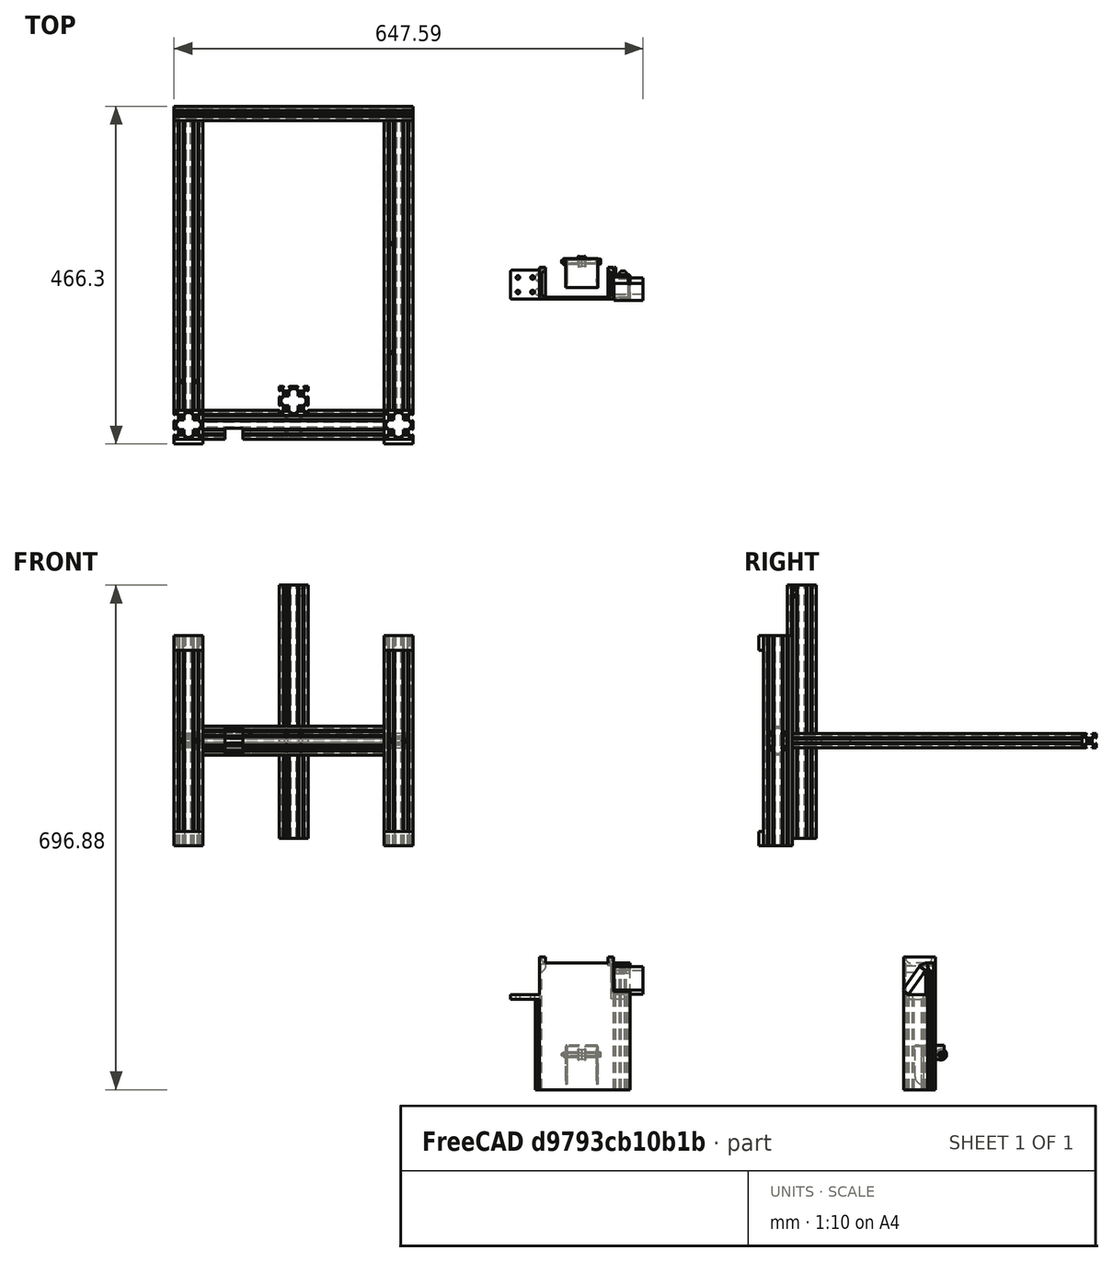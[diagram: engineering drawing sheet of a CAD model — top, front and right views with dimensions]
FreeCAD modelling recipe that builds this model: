
FCSTD DOCUMENT  (FreeCAD 1.1R)
Label: electronic-case-ender3
License: All rights reserved
LicenseURL: https://en.wikipedia.org/wiki/All_rights_reserved
objects: Part::Feature×18, Sketcher::SketchObject×11, PartDesign::Pad×7, PartDesign::Pocket×6, Part::DatumPlane×5, App::Point×3, App::Part×2, PartDesign::SubShapeBinder×2, PartDesign::Fillet×2, Spreadsheet::Sheet×1, Mesh::Feature×1, Part::Box×1, PartDesign::Body×1
note: 89 computed .brp shape members not serialized (recipe doc carries the construction recipe); baked Part::Feature solids carry a one-line shape summary decoded from their .brp

FEATURE [Part::Feature] Part__Feature  label="ЭП-290-4040L"
  Placement = pos=(-524.869,-173.543,336.881) rot=(0,0,1;0rad)
  shape: bbox 40 x 40 x 290 mm, 202 faces (baked)
FEATURE [Part::Feature] Part__Feature001  label="ЭП-290-4040R"
  Placement = pos=(-234.869,-173.543,336.881) rot=(0,0,1;0rad)
  shape: bbox 40 x 40 x 290 mm, 202 faces (baked)
FEATURE [Part::Feature] Part__Feature002  label="ЭП-250-4040D"
  Placement = pos=(-254.869,-173.543,481.881) rot=(0,-1,0;1.5708rad)
  shape: bbox 250 x 40 x 40 mm, 268 faces (baked)
FEATURE [Part::Feature] Part__Feature003  label="ЭП-400-2040L"
  Placement = pos=(-524.869,-153.543,481.881) rot=(-1,0,0;1.5708rad)
  shape: bbox 40 x 400 x 20 mm, 84 faces (baked)
FEATURE [Part::Feature] Part__Feature004  label="ЭП-400-2040R"
  Placement = pos=(-234.869,246.457,481.881) rot=(0,0.707107,-0.707107;3.14159rad)
  shape: bbox 40 x 400 x 20 mm, 92 faces (baked)
FEATURE [Part::Feature] Part__Feature005  label="ЭП-330-2020"
  Placement = pos=(-214.869,256.457,481.881) rot=(0,-1,0;1.5708rad)
  shape: bbox 330 x 20 x 20 mm, 87 faces (baked)
FEATURE [Part::Feature] Part__Feature006  label="ЭП-350-4040C"
  Placement = pos=(-379.869,-140.543,346.881) rot=(0,0,1;0rad)
  shape: bbox 40 x 40 x 350 mm, 142 faces (baked)
FEATURE [Part::Feature] Part__Feature161  label="Дистанционная_шайба_натяжителя"
  Placement = pos=(-1.75288,51.8974,48.5) rot=(0,1,0;1.5708rad)
  shape: bbox 15 x 7.1 x 7.1 mm, 4 faces (baked)
FEATURE [Part::Feature] Part__Feature162  label="Кронштейн_натяжного_ролика"
  Placement = pos=(18.1071,35.9974,59.5) rot=(0,0,1;0rad)
  shape: bbox 44.3 x 40.2 x 54.1 mm, 32 faces (baked)
FEATURE [Part::Feature] Part__Feature163  label="Направляющий_ролик002"
  Placement = pos=(22.9671,51.8974,48.5) rot=(0,-1,0;1.5708rad)
  shape: bbox 4.86 x 15 x 15 mm, 15 faces (baked)
FEATURE [Part::Feature] Part__Feature164  label="Направляющий_ролик003"
  Placement = pos=(13.2471,51.8974,48.5) rot=(0,1,0;1.5708rad)
  shape: bbox 4.86 x 15 x 15 mm, 15 faces (baked)
FEATURE [Part::Feature] Part__Feature165  label="Дистанционная_шайба_натяжителя001"
  Placement = pos=(37.9671,51.8974,48.5) rot=(0,-1,0;1.5708rad)
  shape: bbox 15 x 7.1 x 7.1 mm, 4 faces (baked)
FEATURE [Part::Feature] Part__Feature166  label="CNS 3932 - M 4 x 0,7 x 50"
  Placement = pos=(40.2571,51.8974,48.5) rot=(0,0,1;3.14159rad)
  shape: bbox 54 x 7.577 x 7.577 mm, 15 faces (baked)
FEATURE [Part::Feature] Part__Feature167  label="AS 1112 - M4  Тип 5"
  Placement = pos=(-7.24288,51.8974,48.5) rot=(0,0,1;0rad)
  shape: bbox 3.2 x 8.083 x 8.083 mm, 23 faces (baked)
FEATURE [App::Part] _________________________________________  label="Натяжной_ролик_в_сборе"
  Group = -> [Part__Feature161,Part__Feature162,Part__Feature163,Part__Feature164,Part__Feature165,Part__Feature166,Part__Feature167]
  Origin = -> Origin032
  Placement = pos=(-397.926,-176.441,657.381) rot=(0,0,1;0rad)
FEATURE [App::Point] Origin033
  Role = Origin
FEATURE [Part::Feature] Part__Feature275  label="Резиновые_ножки"
  Placement = pos=(-234.869,-199.843,616.881) rot=(-1,0,0;1.5708rad)
  shape: bbox 40 x 6.3 x 20 mm, 6 faces (baked)
FEATURE [Part::Feature] Part__Feature276  label="Резиновые_ножки001"
  Placement = pos=(-524.869,-193.543,346.881) rot=(1,0,0;1.5708rad)
  shape: bbox 40 x 6.3 x 20 mm, 6 faces (baked)
FEATURE [Part::Feature] Part__Feature277  label="Резиновые_ножки002"
  Placement = pos=(-234.869,-199.843,346.881) rot=(-1,0,0;1.5708rad)
  shape: bbox 40 x 6.3 x 20 mm, 6 faces (baked)
FEATURE [Part::Feature] Part__Feature278  label="Резиновые_ножки003"
  Placement = pos=(-524.869,-193.543,616.881) rot=(1,0,0;1.5708rad)
  shape: bbox 40 x 6.3 x 20 mm, 6 faces (baked)
FEATURE [App::Part] ________  label="Рама"
  Group = -> [Part__Feature,Part__Feature001,Part__Feature002,Part__Feature003,Part__Feature004,Part__Feature005,Part__Feature006,_________________________________________,Part__Feature275,Part__Feature276,Part__Feature277,Part__Feature278]
  Origin = -> Origin052
  Placement = pos=(464.817,193.554,-501.882) rot=(0,0,1;0rad)
FEATURE [App::Point] Origin053
  Role = Origin
FEATURE [App::Point] Origin055
  Role = Origin
FEATURE [Sketcher::SketchObject] Sketch
  ArcFitTolerance = 1e-06
  AttachmentSupport = -> [Origin054]
  ExternalTypes = [0]
  FullyConstrained = false
  MakeInternals = false
  MapMode = 5
  sketch-geometry (56):
    g0: LineSegment StartX=78 StartY=32.9 StartZ=0 EndX=78 EndY=35 EndZ=0
    g1: LineSegment StartX=77.4 StartY=39.1 StartZ=0 EndX=72.6 EndY=39.1 EndZ=0
    g2: LineSegment StartX=70 StartY=35 StartZ=0 EndX=72 EndY=35 EndZ=0
    g3: LineSegment StartX=78 StartY=35 StartZ=0 EndX=80 EndY=35 EndZ=0
    g4: LineSegment StartX=70 StartY=35 StartZ=0 EndX=70 EndY=36.5 EndZ=0
    g5: LineSegment StartX=70 StartY=36.5 StartZ=0 EndX=72.6 EndY=39.1 EndZ=0
    g6: LineSegment StartX=77.4 StartY=39.1 StartZ=0 EndX=80 EndY=36.5 EndZ=0
    g7: LineSegment StartX=80 StartY=36.5 StartZ=0 EndX=80 EndY=35 EndZ=0
    g8: LineSegment [constr] StartX=70 StartY=36.5 StartZ=0 EndX=80 EndY=36.5 EndZ=0
    g9: LineSegment StartX=-40 StartY=11.8 StartZ=0 EndX=-42 EndY=11.8 EndZ=0
    g10: LineSegment StartX=-46.1 StartY=12.1 StartZ=0 EndX=-46.1 EndY=7.6 EndZ=0
    g11: LineSegment StartX=-42 StartY=7.9 StartZ=0 EndX=-40 EndY=7.9 EndZ=0
    g12: LineSegment StartX=-42 StartY=5 StartZ=0 EndX=-43.5 EndY=5 EndZ=0
    g13: LineSegment [constr] StartX=-43.5 StartY=5 StartZ=0 EndX=-43.5 EndY=15 EndZ=0
    g14: LineSegment StartX=-40 StartY=7.9 StartZ=0 EndX=-40 EndY=0 EndZ=0
    g15: LineSegment [constr] StartX=72 StartY=35 StartZ=0 EndX=75 EndY=35 EndZ=0
    g16: LineSegment [constr] StartX=75 StartY=35 StartZ=0 EndX=78 EndY=35 EndZ=0
    g17: LineSegment [constr] StartX=75 StartY=35 StartZ=0 EndX=75 EndY=0 EndZ=0
    g18: LineSegment StartX=-40 StartY=11.8 StartZ=0 EndX=-40 EndY=27.8 EndZ=0
    g19: LineSegment StartX=-37 StartY=16 StartZ=0 EndX=-37 EndY=41.5 EndZ=0
    g20: LineSegment StartX=-40 StartY=44 StartZ=0 EndX=-40 EndY=32 EndZ=0
    g21: LineSegment StartX=-40 StartY=32 StartZ=0 EndX=-42 EndY=32 EndZ=0
    g22: LineSegment StartX=-42 StartY=32 StartZ=0 EndX=-42 EndY=34.9 EndZ=0
    g23: LineSegment StartX=-42 StartY=34.9 StartZ=0 EndX=-43.5 EndY=34.9 EndZ=0
    g24: LineSegment StartX=-43.5 StartY=34.9 StartZ=0 EndX=-46.1 EndY=32.15 EndZ=0
    g25: LineSegment StartX=-46.1 StartY=32.15 StartZ=0 EndX=-46.1 EndY=27.65 EndZ=0
    g26: LineSegment StartX=-46.1 StartY=27.65 StartZ=0 EndX=-43.5 EndY=24.9 EndZ=0
    g27: LineSegment StartX=-43.5 StartY=24.9 StartZ=0 EndX=-42 EndY=24.9 EndZ=0
    g28: LineSegment StartX=-42 StartY=24.9 StartZ=0 EndX=-42 EndY=27.8 EndZ=0
    g29: LineSegment StartX=-42 StartY=27.8 StartZ=0 EndX=-40 EndY=27.8 EndZ=0
    g30: LineSegment StartX=-37 StartY=41.5 StartZ=0 EndX=-38.5 EndY=41.5 EndZ=0
    g31: LineSegment StartX=-38.5 StartY=41.5 StartZ=0 EndX=-38.5 EndY=44 EndZ=0
    g32: LineSegment StartX=-38.5 StartY=44 StartZ=0 EndX=-40 EndY=44 EndZ=0
    g33: LineSegment [constr] StartX=-43.5 StartY=34.9 StartZ=0 EndX=-43.5 EndY=24.9 EndZ=0
    g34: LineSegment StartX=-37 StartY=16 StartZ=0 EndX=-37 EndY=2.5 EndZ=0
    g35: LineSegment StartX=-37 StartY=2.5 StartZ=0 EndX=82.5 EndY=2.5 EndZ=0
    g36: LineSegment [constr] StartX=72 StartY=35 StartZ=0 EndX=72 EndY=2.5 EndZ=0
    g37: LineSegment StartX=63.4 StartY=44 StartZ=0 EndX=64.9 EndY=44 EndZ=0
    g38: LineSegment StartX=64.9 StartY=44 StartZ=0 EndX=64.9 EndY=32.9 EndZ=0
    g39: LineSegment StartX=64.9 StartY=32.9 StartZ=0 EndX=72 EndY=32.9 EndZ=0
    g40: LineSegment StartX=63.4 StartY=44 StartZ=0 EndX=63.4 EndY=41.5 EndZ=0
    g41: LineSegment StartX=63.4 StartY=41.5 StartZ=0 EndX=61.9 EndY=41.5 EndZ=0
    g42: LineSegment StartX=61.9 StartY=41.5 StartZ=0 EndX=61.9 EndY=32.9 EndZ=0
    g43: LineSegment StartX=61.9 StartY=32.9 StartZ=0 EndX=61.9 EndY=30.4 EndZ=0
    g44: LineSegment StartX=61.9 StartY=30.4 StartZ=0 EndX=72 EndY=30.4 EndZ=0
    g45: LineSegment StartX=72 StartY=35 StartZ=0 EndX=72 EndY=32.9 EndZ=0
    g46: LineSegment StartX=78 StartY=32.9 StartZ=0 EndX=85 EndY=32.9 EndZ=0
    g47: LineSegment StartX=85 StartY=32.9 StartZ=0 EndX=85 EndY=0 EndZ=0
    g48: LineSegment StartX=-40 StartY=0 StartZ=0 EndX=85 EndY=0 EndZ=0
    g49: LineSegment StartX=-43.5 StartY=5 StartZ=0 EndX=-46.1 EndY=7.6 EndZ=0
    g50: LineSegment StartX=-46.1 StartY=12.1 StartZ=0 EndX=-43.5 EndY=14.7 EndZ=0
    g51: LineSegment StartX=-43.5 StartY=14.7 StartZ=0 EndX=-42 EndY=14.7 EndZ=0
    g52: LineSegment StartX=-42 StartY=14.7 StartZ=0 EndX=-42 EndY=11.8 EndZ=0
    g53: LineSegment StartX=-42 StartY=7.9 StartZ=0 EndX=-42 EndY=5 EndZ=0
    g54: LineSegment StartX=72 StartY=30.4 StartZ=0 EndX=82.5 EndY=30.4 EndZ=0
    g55: LineSegment StartX=82.5 StartY=30.4 StartZ=0 EndX=82.5 EndY=2.5 EndZ=0
  constraints (164):
    c: Vertical(g0)
    c: Horizontal(g2)
    c: Coincident(g3,g0)
    c: Horizontal(g3,g0)
    c: Horizontal(g0,g2)
    c: Equal(g2,g3)
    c: DistanceX(g2,g3) = 10
    c: Coincident(g4,g2)
    c: Coincident(g4,g5)
    c: Coincident(g5,g1)
    c: Coincident(g6,g1)
    c: Coincident(g6,g7)
    c: Coincident(g7,g3)
    c: Parallel(g7,g4)
    c: Equal(g7,g4)
    c: Angle(g5,g6) = 1.5708
    c: Perpendicular(g2,g4)
    c: Coincident(g8,g4)
    c: Coincident(g8,g6)
    c: Angle(g8,g5) = 0.785398
    c: DistanceY(g7,g7) = 1.5
    c: Horizontal(g1)
    c: Distance(g3,g1) = 4.1
    c: Coincident(g13,g12)
    c: Distance(g9,g10) = 4.1
    c: Coincident(g14,g11)
    c: DistanceX(g11,g11) = 2
    c: Perpendicular(g14,g11)
    c: Vertical(g11,g9)
    c: Distance(g12,g-1) = 5
    c: DistanceY(g12,g13) = 10
    c: Distance(g-1,g14) = 40
    c: Coincident(g15,g2)
    c: Horizontal(g15)
    c: Coincident(g15,g16)
    c: Coincident(g16,g0)
    c: Equal(g15,g16)
    c: Coincident(g17,g15)
    c: Vertical(g17)
    c: Distance(g14,g17) = 115
    c: Equal(g9,g11)
    c: Coincident(g18,g9)
    c: Vertical(g18)
    c: Vertical(g19)
    c: Vertical(g20)
    c: Coincident(g20,g21)
    c: Coincident(g21,g22)
    c: Vertical(g22)
    c: Coincident(g22,g23)
    c: Coincident(g23,g24)
    c: Coincident(g24,g25)
    c: Vertical(g25)
    c: Coincident(g25,g26)
    c: Coincident(g26,g27)
    c: Horizontal(g27)
    c: Coincident(g27,g28)
    c: Coincident(g28,g29)
    c: Coincident(g29,g18)
    c: Perpendicular(g20,g21)
    c: Perpendicular(g18,g29)
    c: Coincident(g30,g19)
    c: Parallel(g30,g23)
    c: Coincident(g30,g31)
    c: Vertical(g31)
    c: Coincident(g31,g32)
    c: Coincident(g32,g20)
    c: Parallel(g32,g30)
    c: Horizontal(g32)
    c: Equal(g30,g32)
    c: Vertical(g18,g20)
    c: Perpendicular(g29,g28)
    c: Coincident(g33,g23)
    c: Coincident(g33,g26)
    c: Vertical(g33)
    c: Equal(g33,g13)
    c: DistanceY(g31,g31) = 2.5
    c: Equal(g24,g26)
    c: Equal(g25,g10)
    c: Vertical(g25,g10)
    c: Vertical(g23,g13)
    c: Vertical(g21,g28)
    c: DistanceY(g18,g18) = 16
    c: DistanceY(g20,g20) = 12
    c: DistanceY(g19,g19) = 25.5
    c: Coincident(g34,g19)
    c: Vertical(g34)
    c: Coincident(g34,g35)
    c: Horizontal(g35)
    c: Coincident(g36,g2)
    c: Parallel(g0,g36)
    c: Distance(g34,g14) = 3
    c: DistanceX(g2,g0) = 6
    c: Perpendicular(g18,g9)
    c: Vertical(g10)
    c: PointOnObject(g44,g36)
    c: Coincident(g37,g38)
    c: Coincident(g38,g39)
    c: PointOnObject(g39,g36)
    c: Horizontal(g39)
    c: Horizontal(g31,g37)
    c: Horizontal(g37)
    c: Vertical(g38)
    c: Coincident(g40,g37)
    c: Vertical(g40)
    c: Coincident(g40,g41)
    c: Coincident(g41,g42)
    c: Vertical(g42)
    c: Coincident(g42,g43)
    c: Vertical(g43)
    c: Coincident(g43,g44)
    c: Perpendicular(g41,g40)
    c: Distance(g38,g42) = 3
    c: Equal(g41,g37)
    c: Distance(g2,g39) = 2.1
    c: DistanceX(g39,g39) = 7.1
    c: Equal(g40,g31)
    c: Horizontal(g42,g38)
    c: DistanceY(g43,g43) = 2.5
    c: Coincident(g45,g2)
    c: Coincident(g45,g39)
    c: Horizontal(g0,g39)
    c: Coincident(g46,g0)
    c: Horizontal(g46)
    c: Coincident(g46,g47)
    c: PointOnObject(g47,g-1)
    c: Vertical(g47)
    c: DistanceX(g17,g47) = 10
    c: Vertical(g14)
    c: PointOnObject(g14,g-1)
    c: Distance(g-1,g35) = 2.5
    c: DistanceY(g38,g38) = 11.1
    c: Coincident(g48,g14)
    c: Coincident(g48,g47)
    c: Coincident(g49,g12)
    c: Coincident(g49,g10)
    c: Coincident(g50,g10)
    c: Distance(g31,g48) = 44
    c: PointOnObject(g17,g48)
    c: DistanceY(g25,g25) = 4.5
    c: Coincident(g51,g50)
    c: Horizontal(g51)
    c: Coincident(g52,g51)
    c: Coincident(g52,g9)
    c: Vertical(g52)
    c: Coincident(g53,g11)
    c: Coincident(g53,g12)
    c: Vertical(g53)
    c: Vertical(g28,g9)
    c: Equal(g53,g52)
    c: Equal(g52,g28)
    c: Perpendicular(g53,g12)
    c: Equal(g49,g50)
    c: Vertical(g13)
    c: Equal(g51,g12)
    c: DistanceX(g51,g51) = 1.5
    c: Equal(g22,g28)
    c: Angle(g13,g49) = 0.785398
    c: Coincident(g54,g44)
    c: Horizontal(g54)
    c: Coincident(g55,g54)
    c: Coincident(g55,g35)
    c: Perpendicular(g55,g54)
    c: Distance(g47,g55) = 2.5
    c: Horizontal(g44)
FEATURE [PartDesign::Pad] Pad
  Direction = (0,0,1)
  Length = 175
  Length2 = 10
  Profile = -> Sketch
  ReferenceAxis = -> Sketch [N_Axis]
  Refine = true
  SideType = 0
  Suppressed = false
  Type = 0
  Type2 = 0
  expr: Length = 125 + Spreadsheet.stickout
FEATURE [Part::DatumPlane] DatumPlane001
  AttachmentSupport = -> [Pad]
  MapMode = 1
  Placement = pos=(-40,44,175) rot=(0,0,1;0rad)
FEATURE [Sketcher::SketchObject] Sketch001
  ArcFitTolerance = 1e-06
  AttachmentSupport = -> [DatumPlane001]
  ExternalTypes = [0]
  FullyConstrained = true
  MakeInternals = false
  MapMode = 5
  Placement = pos=(-40,44,175) rot=(0,0,1;0rad)
  sketch-geometry (10):
    g0: LineSegment StartX=0 StartY=-4 StartZ=0 EndX=-38.5858 EndY=-4 EndZ=0
    g1: LineSegment StartX=-40 StartY=-5.41421 StartZ=0 EndX=-40 EndY=-42.5858 EndZ=0
    g2: LineSegment StartX=-38.5858 StartY=-44 StartZ=0 EndX=0 EndY=-44 EndZ=0
    g3: ArcOfCircle CenterX=-38.5858 CenterY=-5.41421 CenterZ=0 NormalX=0 NormalY=0 NormalZ=1 AngleXU=0 Radius=1.41421 StartAngle=1.5708 EndAngle=3.14159
    g4: GeomPoint [constr] X=-40 Y=-4 Z=0
    g5: LineSegment [constr] StartX=-38.5858 StartY=-4 StartZ=0 EndX=-40 EndY=-5.41421 EndZ=0
    g6: ArcOfCircle CenterX=-38.5858 CenterY=-42.5858 CenterZ=0 NormalX=0 NormalY=0 NormalZ=1 AngleXU=0 Radius=1.41421 StartAngle=3.14159 EndAngle=4.71239
    g7: GeomPoint [constr] X=-40 Y=-44 Z=0
    g8: LineSegment [constr] StartX=-40 StartY=-42.5858 StartZ=0 EndX=-38.5858 EndY=-44 EndZ=0
    g9: LineSegment StartX=0 StartY=-44 StartZ=0 EndX=0 EndY=-4 EndZ=0
  constraints (24):
    c: Horizontal(g0)
    c: Horizontal(g2)
    c: Vertical(g1)
    c: DistanceY(g7,g4) = 40
    c: PointOnObject(g4,g0)
    c: PointOnObject(g4,g1)
    c: Tangent(g0,g3) = -1.5708
    c: Tangent(g1,g3) = -1.5708
    c: Coincident(g5,g0)
    c: Coincident(g5,g1)
    c: PointOnObject(g7,g1)
    c: PointOnObject(g7,g2)
    c: Tangent(g1,g6) = -1.5708
    c: Tangent(g2,g6) = -1.5708
    c: Coincident(g8,g1)
    c: Coincident(g8,g2)
    c: Equal(g8,g5)
    c: Distance(g5,g5) = 2
    c: DistanceX(g7,g2) = 40
    c: Coincident(g9,g2)
    c: PointOnObject(g9,g-2)
    c: Vertical(g9)
    c: Coincident(g0,g9)
    c: Distance(g-1,g0) = 4
FEATURE [PartDesign::Pad] Pad001
  BaseFeature = -> Pad
  Direction = (0,0,1)
  Length = 50.001
  Length2 = 10
  Profile = -> Sketch001
  ReferenceAxis = -> Sketch001 [N_Axis]
  Refine = true
  Reversed = true
  SideType = 0
  Suppressed = false
  Type = 0
  Type2 = 0
  expr: Length = Spreadsheet.stickout + 0.001
FEATURE [Sketcher::SketchObject] Sketch002
  ArcFitTolerance = 1e-06
  AttachmentSupport = -> [DatumPlane001]
  ExternalTypes = [0]
  FullyConstrained = true
  MakeInternals = false
  MapMode = 5
  Placement = pos=(-40,44,175) rot=(0,0,1;0rad)
  sketch-geometry (4):
    g0: LineSegment StartX=0 StartY=0 StartZ=0 EndX=-44 EndY=0 EndZ=0
    g1: LineSegment StartX=-44 StartY=0 StartZ=0 EndX=-44 EndY=-44 EndZ=0
    g2: LineSegment StartX=-44 StartY=-44 StartZ=0 EndX=0 EndY=-44 EndZ=0
    g3: LineSegment StartX=0 StartY=-44 StartZ=0 EndX=0 EndY=0 EndZ=0
  constraints (11):
    c: Coincident(g0,g1)
    c: Coincident(g1,g2)
    c: Coincident(g2,g3)
    c: Coincident(g3,g0)
    c: Horizontal(g0)
    c: Horizontal(g2)
    c: Vertical(g1)
    c: Vertical(g3)
    c: Coincident(g0,g-1)
    c: Equal(g1,g0)
    c: DistanceY(g1,g1) = 44
FEATURE [Spreadsheet::Sheet] Spreadsheet
  cells = B1(stickout)=50
FEATURE [PartDesign::Pocket] Pocket
  BaseFeature = -> Pad001
  Direction = (0,0,-1)
  Length = 44.001
  Length2 = 5
  Profile = -> Sketch002
  ReferenceAxis = -> Sketch002 [N_Axis]
  Refine = true
  SideType = 0
  Suppressed = false
  Type = 0
  Type2 = 0
  expr: Length = Spreadsheet.stickout - 6 + 0.001
FEATURE [Sketcher::SketchObject] Sketch003
  ArcFitTolerance = 1e-06
  AttachmentSupport = -> [DatumPlane001]
  ExternalTypes = [0]
  FullyConstrained = true
  MakeInternals = false
  MapMode = 5
  Placement = pos=(-40,44,175) rot=(0,0,1;0rad)
  sketch-geometry (8):
    g0: Circle CenterX=-10 CenterY=-14 CenterZ=0 NormalX=0 NormalY=0 NormalZ=1 AngleXU=0 Radius=2.5
    g1: Circle CenterX=-30 CenterY=-14 CenterZ=0 NormalX=0 NormalY=0 NormalZ=1 AngleXU=0 Radius=2.5
    g2: Circle CenterX=-30 CenterY=-34 CenterZ=0 NormalX=0 NormalY=0 NormalZ=1 AngleXU=0 Radius=2.5
    g3: Circle CenterX=-10 CenterY=-34 CenterZ=0 NormalX=0 NormalY=0 NormalZ=1 AngleXU=0 Radius=2.5
    g4: LineSegment [constr] StartX=-30 StartY=-14 StartZ=0 EndX=-10 EndY=-14 EndZ=0
    g5: LineSegment [constr] StartX=-10 StartY=-14 StartZ=0 EndX=-10 EndY=-34 EndZ=0
    g6: LineSegment [constr] StartX=-10 StartY=-34 StartZ=0 EndX=-30 EndY=-34 EndZ=0
    g7: LineSegment [constr] StartX=-30 StartY=-34 StartZ=0 EndX=-30 EndY=-14 EndZ=0
  constraints (20):
    c: Diameter(g0) = 5
    c: Equal(g1,g0)
    c: Equal(g0,g3)
    c: Equal(g3,g2)
    c: Coincident(g4,g1)
    c: Coincident(g4,g0)
    c: Horizontal(g4)
    c: Coincident(g4,g5)
    c: Coincident(g5,g3)
    c: Vertical(g5)
    c: Coincident(g5,g6)
    c: Coincident(g6,g2)
    c: Horizontal(g6)
    c: Coincident(g6,g7)
    c: Coincident(g7,g1)
    c: Vertical(g7)
    c: Equal(g7,g4)
    c: Distance(g0,g-2) = 10
    c: Distance(g0,g-1) = 14
    c: DistanceX(g4,g4) = 20
FEATURE [PartDesign::Pocket] Pocket001
  BaseFeature = -> Pocket
  Direction = (0,0,-1)
  Length = 500
  Length2 = 5
  Profile = -> Sketch003
  ReferenceAxis = -> Sketch003 [N_Axis]
  Refine = true
  SideType = 0
  Suppressed = false
  Type = 0
  Type2 = 0
FEATURE [Mesh::Feature] Headless_Skirt_Insert
  Placement = pos=(-207.979,-60.019,-95.105) rot=(0,0,1;0rad)
FEATURE [PartDesign::SubShapeBinder] Binder
  BindCopyOnChange = 0
  BindMode = 0
  ClaimChildren = false
  Context = -> Body [Pad003.Binder.]
  Fuse = false
  MakeFace = true
  OffsetFill = false
  OffsetIntersection = false
  OffsetJoinType = 0
  OffsetOpenResult = false
  PartialLoad = false
  Placement = pos=(102,0,0) rot=(0,0,1;0rad)
  Relative = true
  Support = -> [Sketch005]
  _Version = 2
FEATURE [PartDesign::SubShapeBinder] Binder001
  BindCopyOnChange = 0
  BindMode = 0
  ClaimChildren = false
  Context = -> Body [Binder001.]
  Fuse = false
  MakeFace = true
  OffsetFill = false
  OffsetIntersection = false
  OffsetJoinType = 0
  OffsetOpenResult = false
  PartialLoad = false
  Placement = pos=(86,0,0) rot=(0,0,1;0rad)
  Refine = true
  Relative = true
  Support = -> [Sketch006]
  _Version = 2
FEATURE [Part::Box] Box  label="Cube"
  AttacherType = Attacher::AttachEngine3D
  Height = 40
  Length = 10
  Placement = pos=(102.724,21.5401,170.201) rot=(0.663579,0.345437,-0.663579;3.8068rad)
  Width = 40
FEATURE [Part::DatumPlane] DatumPlane
  AttachmentOffset = pos=(0,0,0) rot=(0.57735,0.57735,0.57735;2.0944rad)
  AttachmentSupport = -> [Pocket001]
  MapMode = 7
  Placement = pos=(-40,0,175) rot=(0.57735,0.57735,0.57735;2.0944rad)
FEATURE [Sketcher::SketchObject] Sketch005
  ArcFitTolerance = 1e-06
  AttachmentSupport = -> [DatumPlane]
  ExternalTypes = [0]
  FullyConstrained = true
  MakeInternals = false
  MapMode = 5
  Placement = pos=(-40,0,175) rot=(0.57735,0.57735,0.57735;2.0944rad)
  sketch-geometry (8):
    g0: LineSegment [constr] StartX=0 StartY=-4 StartZ=0 EndX=44 EndY=-4 EndZ=0
    g1: LineSegment [constr] StartX=44 StartY=-4 StartZ=0 EndX=44 EndY=8 EndZ=0
    g2: LineSegment StartX=44 StartY=8 StartZ=0 EndX=0 EndY=8 EndZ=0
    g3: LineSegment StartX=0 StartY=8 StartZ=0 EndX=0 EndY=-4 EndZ=0
    g4: LineSegment StartX=0 StartY=-4 StartZ=0 EndX=41.5 EndY=-4 EndZ=0
    g5: LineSegment StartX=41.5 StartY=-4 StartZ=0 EndX=41.5 EndY=-1 EndZ=0
    g6: LineSegment StartX=41.5 StartY=-1 StartZ=0 EndX=44 EndY=-1 EndZ=0
    g7: LineSegment StartX=44 StartY=-1 StartZ=0 EndX=44 EndY=8 EndZ=0
  constraints (23):
    c: Coincident(g0,g1)
    c: Coincident(g1,g2)
    c: Coincident(g2,g3)
    c: Coincident(g3,g0)
    c: Horizontal(g0)
    c: Horizontal(g2)
    c: Vertical(g1)
    c: Vertical(g3)
    c: PointOnObject(g0,g-2)
    c: DistanceY(g1,g1) = 12
    c: Distance(g-1,g0) = 4
    c: DistanceX(g2,g2) = 44
    c: Coincident(g4,g0)
    c: PointOnObject(g4,g0)
    c: Coincident(g4,g5)
    c: Vertical(g5)
    c: Coincident(g5,g6)
    c: PointOnObject(g6,g1)
    c: Horizontal(g6)
    c: Coincident(g6,g7)
    c: Coincident(g7,g1)
    c: Distance(g6,g0) = 3
    c: DistanceX(g6,g6) = 2.5
FEATURE [PartDesign::Pad] Pad002
  BaseFeature = -> Pocket001
  Direction = (1,0,0)
  Length = 8
  Length2 = 10
  Profile = -> Sketch005
  ReferenceAxis = -> Sketch005 [N_Axis]
  Refine = true
  SideType = 0
  Suppressed = false
  Type = 0
  Type2 = 0
FEATURE [PartDesign::Pad] Pad003
  BaseFeature = -> Pad002
  Direction = (1,0,0)
  Length = 8
  Length2 = 10
  Profile = -> Binder
  Refine = true
  Reversed = true
  SideType = 0
  Suppressed = false
  Type = 0
  Type2 = 0
FEATURE [Sketcher::SketchObject] Sketch006
  ArcFitTolerance = 1e-06
  AttachmentOffset = pos=(0,0,8) rot=(0,0,1;0rad)
  AttachmentSupport = -> [DatumPlane]
  ExternalTypes = [0]
  FullyConstrained = true
  MakeInternals = false
  MapMode = 5
  Placement = pos=(-32,0,175) rot=(0.57735,0.57735,0.57735;2.0944rad)
  sketch-geometry (6):
    g0: ArcOfCircle CenterX=32.5 CenterY=6.5 CenterZ=0 NormalX=0 NormalY=0 NormalZ=1 AngleXU=0 Radius=6.5 StartAngle=4.71239 EndAngle=6.28319
    g1: ArcOfCircle CenterX=9.5 CenterY=6.5 CenterZ=0 NormalX=0 NormalY=0 NormalZ=1 AngleXU=0 Radius=6.5 StartAngle=3.14159 EndAngle=4.71239
    g2: LineSegment StartX=39 StartY=6.5 StartZ=0 EndX=39 EndY=8 EndZ=0
    g3: LineSegment StartX=39 StartY=8 StartZ=0 EndX=3 EndY=8 EndZ=0
    g4: LineSegment StartX=3 StartY=8 StartZ=0 EndX=3 EndY=6.5 EndZ=0
    g5: LineSegment StartX=32.5 StartY=0 StartZ=0 EndX=9.5 EndY=0 EndZ=0
  constraints (16):
    c: Vertical(g2)
    c: Coincident(g2,g3)
    c: Horizontal(g3)
    c: Coincident(g3,g4)
    c: DistanceX(g3,g3) = 36
    c: Vertical(g4)
    c: Equal(g4,g2)
    c: Tangent(g1,g-1) = -1.5708
    c: Tangent(g2,g0) = -1.5708
    c: Tangent(g4,g1) = -1.5708
    c: Tangent(g0,g-1) = -1.5708
    c: Distance(g2,g-1) = 8
    c: Distance(g2,g2) = 1.5
    c: Distance(g3,g-2) = 3
    c: Tangent(g5,g0) = 1.5708
    c: Coincident(g5,g1)
FEATURE [PartDesign::Pocket] Pocket003
  BaseFeature = -> Pad003
  Direction = (-1,0,0)
  Length = 5
  Length2 = 5
  Profile = -> Sketch006
  ReferenceAxis = -> Sketch006 [N_Axis]
  Refine = true
  SideType = 0
  Suppressed = false
  Type = 0
  Type2 = 0
FEATURE [PartDesign::Pocket] Pocket004
  BaseFeature = -> Pocket003
  Direction = (-1,0,0)
  Length = 5
  Length2 = 5
  Profile = -> Binder001
  Refine = true
  Reversed = true
  SideType = 0
  Suppressed = false
  Type = 0
  Type2 = 0
FEATURE [PartDesign::Fillet] Fillet001
  Base = -> Pocket004 [Edge226]
  BaseFeature = -> Pocket004
  Radius = 4.8
  Refine = true
  SupportTransform = false
  Suppressed = false
  UseAllEdges = false
FEATURE [PartDesign::Fillet] Fillet
  Base = -> Fillet001 [Edge245]
  BaseFeature = -> Fillet001
  Radius = 4.8
  Refine = true
  SupportTransform = false
  Suppressed = false
  UseAllEdges = false
FEATURE [Part::DatumPlane] DatumPlane002
  AttachmentOffset = pos=(0,0,0) rot=(0,1,0;1.5708rad)
  AttachmentSupport = -> [Fillet]
  MapMode = 7
  Placement = pos=(85,32.9,0) rot=(-0.57735,0.57735,0.57735;4.18879rad)
FEATURE [Sketcher::SketchObject] Sketch007
  ArcFitTolerance = 1e-06
  AttachmentSupport = -> [DatumPlane002]
  ExternalTypes = [0]
  FullyConstrained = true
  MakeInternals = false
  MapMode = 5
  Placement = pos=(85,32.9,0) rot=(0.57735,-0.57735,-0.57735;2.0944rad)
  expr: Constraints[11] = 125 + Spreadsheet.stickout
  sketch-geometry (21):
    g0: LineSegment [constr] StartX=36.9 StartY=0 StartZ=0 EndX=36.9 EndY=175 EndZ=0
    g1: LineSegment [constr] StartX=36.9 StartY=175 StartZ=0 EndX=0 EndY=175 EndZ=0
    g2: LineSegment [constr] StartX=0 StartY=175 StartZ=0 EndX=0 EndY=0 EndZ=0
    g3: LineSegment [constr] StartX=0 StartY=0 StartZ=0 EndX=36.9 EndY=0 EndZ=0
    g4: LineSegment StartX=11.5107 StartY=171 StartZ=0 EndX=2.5 EndY=164.691 EndZ=0
    g5: LineSegment [constr] StartX=2.5 StartY=164.691 StartZ=0 EndX=26.0166 EndY=131.105 EndZ=0
    g6: LineSegment StartX=26.0166 StartY=131.105 StartZ=0 EndX=35.0273 EndY=137.415 EndZ=0
    g7: LineSegment StartX=35.0273 StartY=137.415 StartZ=0 EndX=36.9 EndY=134.74 EndZ=0
    g8: LineSegment [constr] StartX=35.0273 StartY=137.415 StartZ=0 EndX=11.5107 EndY=171 EndZ=0
    g9: LineSegment StartX=2.5 StartY=189.74 StartZ=0 EndX=36.9 EndY=189.74 EndZ=0
    g10: LineSegment StartX=36.9 StartY=189.74 StartZ=0 EndX=36.9 EndY=134.74 EndZ=0
    g11: LineSegment [constr] StartX=11.5107 StartY=171 StartZ=0 EndX=11.5107 EndY=175 EndZ=0
    g12: LineSegment [constr] StartX=11.5107 StartY=175 StartZ=0 EndX=2.5 EndY=175 EndZ=0
    g13: LineSegment StartX=2.5 StartY=175 StartZ=0 EndX=2.5 EndY=189.74 EndZ=0
    g14: LineSegment [constr] StartX=0 StartY=125 StartZ=0 EndX=0 EndY=30 EndZ=0
    g15: LineSegment [constr] StartX=0 StartY=30 StartZ=0 EndX=34.4 EndY=30 EndZ=0
    g16: LineSegment [constr] StartX=34.4 StartY=30 StartZ=0 EndX=34.4 EndY=125 EndZ=0
    g17: LineSegment [constr] StartX=34.4 StartY=125 StartZ=0 EndX=0 EndY=125 EndZ=0
    g18: LineSegment StartX=26.0166 StartY=131.105 StartZ=0 EndX=2.5 EndY=131.105 EndZ=0
    g19: LineSegment StartX=2.5 StartY=131.105 StartZ=0 EndX=2.5 EndY=164.691 EndZ=0
    g20: LineSegment StartX=11.5107 StartY=171 StartZ=0 EndX=2.5 EndY=175 EndZ=0
  constraints (60):
    c: Coincident(g0,g1)
    c: Coincident(g1,g2)
    c: Coincident(g2,g3)
    c: Coincident(g3,g0)
    c: Vertical(g0)
    c: Vertical(g2)
    c: Horizontal(g1)
    c: Horizontal(g3)
    c: PointOnObject(g0,g-1)
    c: PointOnObject(g1,g-2)
    c: DistanceX(g3,g3) = 36.9
    c: DistanceY(g2,g2) = 175
    c: Coincident(g4,g5)
    c: Perpendicular(g5,g4)
    c: Coincident(g5,g6)
    c: Perpendicular(g6,g5)
    c: Coincident(g6,g7)
    c: PointOnObject(g7,g0)
    c: Perpendicular(g7,g6)
    c: Distance(g6,g6) = 11
    c: Distance(g5,g5) = 41
    c: Coincident(g8,g6)
    c: Coincident(g8,g4)
    c: Parallel(g8,g5)
    c: Distance(g4,g2) = 2.5
    c: Horizontal(g9)
    c: Coincident(g9,g10)
    c: Coincident(g10,g7)
    c: Vertical(g10)
    c: DistanceY(g10,g10) = 55
    c: Coincident(g11,g4)
    c: PointOnObject(g11,g1)
    c: Vertical(g11)
    c: Coincident(g11,g12)
    c: PointOnObject(g12,g1)
    c: Coincident(g12,g13)
    c: Vertical(g13)
    c: Vertical(g4,g12)
    c: Coincident(g9,g13)
    c: Angle(g12,g4) = 0.610865
    c: Distance(g11,g11) = 4
    c: Coincident(g14,g15)
    c: Coincident(g15,g16)
    c: Coincident(g16,g17)
    c: Coincident(g17,g14)
    c: Vertical(g14)
    c: Vertical(g16)
    c: Horizontal(g15)
    c: Horizontal(g17)
    c: PointOnObject(g14,g2)
    c: Distance(g16,g0) = 2.5
    c: Distance(g3,g15) = 30
    c: Distance(g-1,g17) = 125
    c: Coincident(g18,g5)
    c: Horizontal(g18)
    c: Coincident(g18,g19)
    c: Coincident(g19,g4)
    c: Vertical(g19)
    c: Coincident(g20,g4)
    c: Coincident(g20,g12)
FEATURE [PartDesign::Pocket] Pocket005
  BaseFeature = -> Fillet
  Direction = (1,0,0)
  Length = 23
  Length2 = 5
  Profile = -> Sketch007
  ReferenceAxis = -> Sketch007 [N_Axis]
  Refine = true
  Reversed = true
  SideType = 0
  Suppressed = false
  Type = 0
  Type2 = 0
FEATURE [Part::DatumPlane] DatumPlane003
  AttachmentOffset = pos=(0,0,0) rot=(0,1,0;1.5708rad)
  AttachmentSupport = -> [Pocket005]
  MapMode = 7
  Placement = pos=(-37,2.5,171) rot=(1,0,0;1.5708rad)
FEATURE [Sketcher::SketchObject] Sketch008
  ArcFitTolerance = 1e-06
  AttachmentSupport = -> [DatumPlane003]
  ExternalTypes = [0]
  FullyConstrained = false
  MakeInternals = false
  MapMode = 5
  Placement = pos=(-37,2.5,171) rot=(1,0,0;1.5708rad)
  sketch-geometry (6):
    g0: LineSegment StartX=5 StartY=0 StartZ=0 EndX=0 EndY=0 EndZ=0
    g1: LineSegment StartX=0 StartY=0 StartZ=0 EndX=0 EndY=-8.53553 EndZ=0
    g2: LineSegment StartX=5 StartY=0 StartZ=0 EndX=5 EndY=-2.5377 EndZ=0
    g3: LineSegment StartX=4.29442 StartY=-4.24111 StartZ=0 EndX=0 EndY=-8.53553 EndZ=0
    g4: ArcOfCircle CenterX=2.59101 CenterY=-2.5377 CenterZ=0 NormalX=0 NormalY=0 NormalZ=1 AngleXU=0 Radius=2.40899 StartAngle=5.49779 EndAngle=6.28319
    g5: GeomPoint [constr] X=5 Y=-3.53553 Z=0
  constraints (13):
    c: PointOnObject(g0,g-1)
    c: Coincident(g0,g-1)
    c: Coincident(g0,g1)
    c: PointOnObject(g1,g-2)
    c: Coincident(g2,g0)
    c: Vertical(g2)
    c: DistanceX(g0,g0) = 5
    c: Coincident(g3,g1)
    c: Angle(g3,g1) = 0.785398
    c: PointOnObject(g5,g2)
    c: PointOnObject(g5,g3)
    c: Tangent(g2,g4) = 1.5708
    c: Tangent(g3,g4) = 1.5708
FEATURE [PartDesign::Pad] Pad004
  BaseFeature = -> Pocket005
  Direction = (0,-1,2e-16)
  Length = 39
  Length2 = 10
  Profile = -> Sketch008
  ReferenceAxis = -> Sketch008 [N_Axis]
  Refine = true
  Reversed = true
  SideType = 0
  Suppressed = false
  Type = 0
  Type2 = 0
FEATURE [Part::DatumPlane] DatumPlane004
  AttachmentOffset = pos=(0,0,0) rot=(0.57735,0.57735,0.57735;2.0944rad)
  AttachmentSupport = -> [Pad004]
  MapMode = 7
  Placement = pos=(62,2.5,171) rot=(0.57735,0.57735,0.57735;2.0944rad)
FEATURE [Sketcher::SketchObject] Sketch009
  ArcFitTolerance = 1e-06
  AttachmentSupport = -> [DatumPlane004]
  ExternalTypes = [0]
  FullyConstrained = true
  MakeInternals = false
  MapMode = 5
  Placement = pos=(62,2.5,171) rot=(0.57735,0.57735,0.57735;2.0944rad)
  expr: Constraints[15] = Spreadsheet.stickout - 4
  sketch-geometry (6):
    g0: LineSegment [constr] StartX=0 StartY=0 StartZ=0 EndX=0 EndY=-45.7008 EndZ=0
    g1: LineSegment [constr] StartX=0 StartY=-45.7008 StartZ=0 EndX=32 EndY=0 EndZ=0
    g2: LineSegment StartX=32 StartY=0 StartZ=0 EndX=0 EndY=0 EndZ=0
    g3: LineSegment StartX=0 StartY=0 StartZ=0 EndX=0 EndY=-46 EndZ=0
    g4: LineSegment StartX=0 StartY=-46 StartZ=0 EndX=-0.20953 EndY=-46 EndZ=0
    g5: LineSegment StartX=-0.20953 StartY=-46 StartZ=0 EndX=32 EndY=0 EndZ=0
  constraints (16):
    c: Coincident(g0,g-1)
    c: PointOnObject(g0,g-2)
    c: Coincident(g1,g0)
    c: PointOnObject(g1,g-1)
    c: Angle(g1,g0) = 0.610865
    c: Coincident(g2,g1)
    c: Coincident(g2,g0)
    c: DistanceX(g2,g2) = 32
    c: Coincident(g3,g0)
    c: PointOnObject(g3,g0)
    c: Coincident(g3,g4)
    c: PointOnObject(g4,g1)
    c: Horizontal(g4)
    c: Coincident(g4,g5)
    c: Coincident(g5,g1)
    c: DistanceY(g3,g3) = 46
FEATURE [PartDesign::Pad] Pad005
  BaseFeature = -> Pad004
  Direction = (1,0,0)
  Length = 3
  Length2 = 10
  Profile = -> Sketch009
  ReferenceAxis = -> Sketch009 [N_Axis]
  Refine = true
  Reversed = true
  SideType = 0
  Suppressed = false
  Type = 0
  Type2 = 0
FEATURE [Sketcher::SketchObject] Sketch010
  ArcFitTolerance = 1e-06
  AttachmentSupport = -> [DatumPlane002]
  ExternalTypes = [0]
  FullyConstrained = true
  MakeInternals = false
  MapMode = 5
  Placement = pos=(85,32.9,0) rot=(0.57735,-0.57735,-0.57735;2.0944rad)
  sketch-geometry (4):
    g0: ArcOfCircle CenterX=-11 CenterY=173 CenterZ=0 NormalX=0 NormalY=0 NormalZ=1 AngleXU=0 Radius=11 StartAngle=3.14159 EndAngle=6.28319
    g1: LineSegment StartX=-22 StartY=173 StartZ=0 EndX=-22 EndY=195 EndZ=0
    g2: LineSegment StartX=-22 StartY=195 StartZ=0 EndX=0 EndY=195 EndZ=0
    g3: LineSegment StartX=0 StartY=195 StartZ=0 EndX=0 EndY=173 EndZ=0
  constraints (12):
    c: PointOnObject(g0,g-2)
    c: Coincident(g1,g0)
    c: Vertical(g1)
    c: Coincident(g2,g1)
    c: Horizontal(g2)
    c: Coincident(g2,g3)
    c: Tangent(g3,g0) = 1.5708
    c: DistanceX(g2,g2) = 22
    c: PointOnObject(g2,g-2)
    c: Horizontal(g0,g0)
    c: DistanceY(g3,g3) = 22
    c: Distance(g-1,g2) = 195
FEATURE [PartDesign::Pocket] Pocket006
  BaseFeature = -> Pad005
  Direction = (1,-1e-16,1e-16)
  Length = 22.2
  Length2 = 5
  Profile = -> Sketch010
  ReferenceAxis = -> Sketch010 [N_Axis]
  Refine = true
  Reversed = true
  SideType = 0
  Suppressed = false
  Type = 0
  Type2 = 0
FEATURE [Sketcher::SketchObject] Sketch011
  ArcFitTolerance = 1e-06
  AttachmentSupport = -> [DatumPlane004]
  ExternalTypes = [0]
  FullyConstrained = false
  MakeInternals = false
  MapMode = 5
  Placement = pos=(62,2.5,171) rot=(0.57735,0.57735,0.57735;2.0944rad)
  sketch-geometry (12):
    g0: LineSegment StartX=27.915 StartY=4 StartZ=0 EndX=19.6317 EndY=0 EndZ=0
    g1: LineSegment StartX=19.6317 StartY=0 StartZ=0 EndX=27.915 EndY=-5.8 EndZ=0
    g2: LineSegment StartX=4.39836 StartY=-39.3852 StartZ=0 EndX=0 EndY=-36.3055 EndZ=0
    g3: LineSegment StartX=0 StartY=-36.3055 StartZ=0 EndX=0 EndY=-45.6667 EndZ=0
    g4: LineSegment StartX=0 StartY=-45.6667 StartZ=0 EndX=4.39836 EndY=-39.3852 EndZ=0
    g5: LineSegment StartX=27.915 StartY=4 StartZ=0 EndX=27.915 EndY=-5.8 EndZ=0
    g6: LineSegment [constr] StartX=27.915 StartY=-5.8 StartZ=0 EndX=4.39836 EndY=-39.3852 EndZ=0
    g7: LineSegment StartX=27.3404 StartY=-6.62057 StartZ=0 EndX=24.7262 EndY=-10.3541 EndZ=0
    g8: LineSegment StartX=24.7262 StartY=-10.3541 StartZ=0 EndX=31.3404 EndY=-10.3541 EndZ=0
    g9: LineSegment StartX=31.3404 StartY=-10.3541 StartZ=0 EndX=31.3404 EndY=0 EndZ=0
    g10: LineSegment StartX=31.3404 StartY=0 StartZ=0 EndX=27.3404 EndY=0 EndZ=0
    g11: LineSegment StartX=27.3404 StartY=0 StartZ=0 EndX=27.3404 EndY=-6.62057 EndZ=0
  constraints (33):
    c: PointOnObject(g0,g-1)
    c: Coincident(g0,g1)
    c: PointOnObject(g2,g-2)
    c: Parallel(g2,g1)
    c: Coincident(g2,g3)
    c: PointOnObject(g3,g-2)
    c: Coincident(g3,g4)
    c: Coincident(g4,g2)
    c: Perpendicular(g4,g2)
    c: Coincident(g5,g0)
    c: Coincident(g5,g1)
    c: Vertical(g5)
    c: Angle(g5,g1) = 0.959931
    c: Distance(g0,g-1) = 4
    c: Distance(g-2,g5) = 27.915
    c: Coincident(g6,g1)
    c: Coincident(g6,g2)
    c: Parallel(g6,g4)
    c: Distance(g6,g6) = 41
    c: Distance(g1,g-1) = 5.8
    c: PointOnObject(g7,g6)
    c: PointOnObject(g7,g6)
    c: Coincident(g7,g8)
    c: Horizontal(g8)
    c: Coincident(g8,g9)
    c: PointOnObject(g9,g-1)
    c: Vertical(g9)
    c: Coincident(g9,g10)
    c: PointOnObject(g10,g-1)
    c: Coincident(g10,g11)
    c: Coincident(g11,g7)
    c: Parallel(g11,g9)
    c: DistanceX(g10,g10) = 4
FEATURE [PartDesign::Pad] Pad006
  BaseFeature = -> Pocket006
  Direction = (1,0,0)
  Length = 22
  Length2 = 3
  Profile = -> Sketch011
  ReferenceAxis = -> Sketch011 [N_Axis]
  Refine = true
  SideType = 1
  Suppressed = false
  Type = 0
  Type2 = 0
FEATURE [PartDesign::Body] Body
  AllowCompound = false
  Group = -> [Sketch,Pad,DatumPlane001,Sketch001,Pad001,Sketch002,Pocket,Sketch003,Pocket001,Sketch005,Binder,Pad002,Pad003,Sketch006,Binder001,Pocket003,Pocket004,Fillet001,DatumPlane,Fillet,DatumPlane002,Sketch007,Pocket005,DatumPlane003,Sketch008,Pad004,DatumPlane004,Sketch009,Pad005,Sketch010,Pocket006,Sketch011,Pad006]
  Origin = -> Origin054
  Tip = -> Pad006
